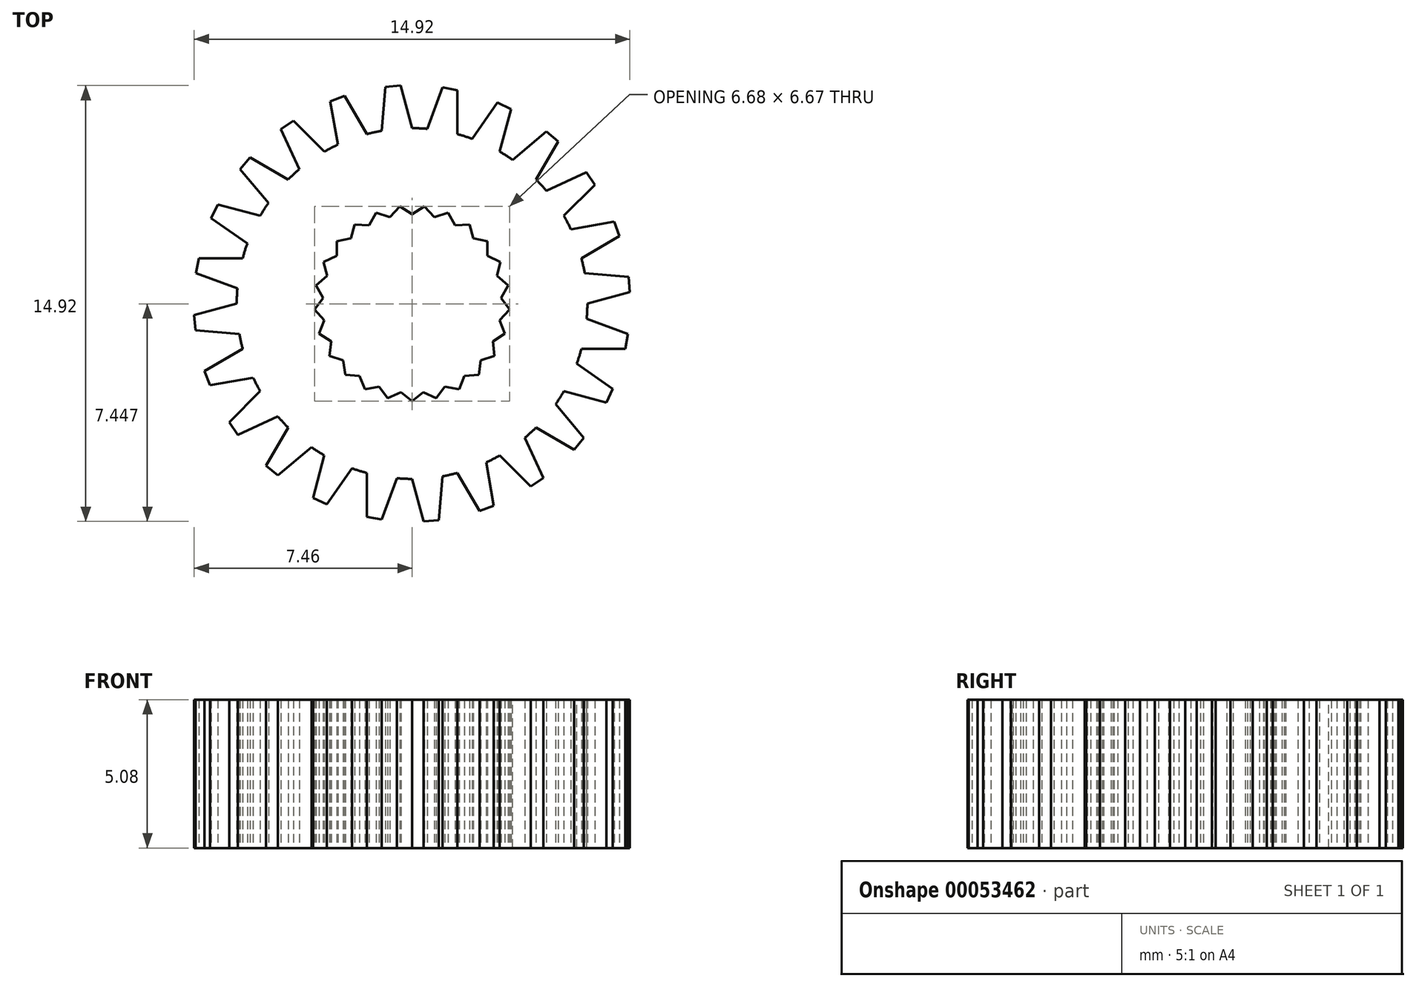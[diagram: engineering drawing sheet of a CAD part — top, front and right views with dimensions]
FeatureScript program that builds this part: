
annotation { "Feature Type Name" : "Feature", "Feature Type Description" : "" }
export const myFeature = defineFeature(function(context is Context, id is Id, definition is map)
    precondition{}
    {
        {
            var Q0;
            Q0=qCreatedBy(makeId("Top.planeOp"),FACE);
            var sketch = newSketch(context, id + "F0", { "sketchPlane" : qUnion([Q0])});
            skArc(sketch, "E0", {"start": v(0.52, 5.98) * mm, "mid": v(0.26, 6) * mm, "end": v(0, 6) * mm});
            skLineSegment(sketch, "E1", {"start": v(0, 6) * mm, "end": v(-0.39, 7.46) * mm});
            skLineSegment(sketch, "E2", {"start": v(-0.91, 7.41) * mm, "end": v(-0.39, 7.46) * mm});
            skLineSegment(sketch, "E3", {"start": v(-1.04, 5.91) * mm, "end": v(-0.91, 7.41) * mm});
            skLineSegment(sketch, "E4", {"start": v(-1.55, 5.8) * mm, "end": v(-2.3, 7.1) * mm});
            skLineSegment(sketch, "E5", {"start": v(-2.8, 6.93) * mm, "end": v(-2.3, 7.1) * mm});
            skLineSegment(sketch, "E6", {"start": v(-2.54, 5.44) * mm, "end": v(-2.8, 6.93) * mm});
            skLineSegment(sketch, "E7", {"start": v(-3, 5.2) * mm, "end": v(-4.07, 6.27) * mm});
            skLineSegment(sketch, "E8", {"start": v(-4.5, 5.97) * mm, "end": v(-4.07, 6.27) * mm});
            skLineSegment(sketch, "E9", {"start": v(-3.86, 4.6) * mm, "end": v(-4.5, 5.97) * mm});
            skLineSegment(sketch, "E10", {"start": v(-4.25, 4.25) * mm, "end": v(-5.55, 5) * mm});
            skLineSegment(sketch, "E11", {"start": v(-5.89, 4.6) * mm, "end": v(-5.55, 5) * mm});
            skLineSegment(sketch, "E12", {"start": v(-4.92, 3.44) * mm, "end": v(-5.89, 4.6) * mm});
            skLineSegment(sketch, "E13", {"start": v(-5.2, 3) * mm, "end": v(-6.66, 3.4) * mm});
            skLineSegment(sketch, "E14", {"start": v(-6.88, 2.92) * mm, "end": v(-6.66, 3.4) * mm});
            skLineSegment(sketch, "E15", {"start": v(-5.64, 2.05) * mm, "end": v(-6.88, 2.92) * mm});
            skLineSegment(sketch, "E16", {"start": v(-5.8, 1.55) * mm, "end": v(-7.3, 1.55) * mm});
            skLineSegment(sketch, "E17", {"start": v(-7.4, 1.04) * mm, "end": v(-7.3, 1.55) * mm});
            skLineSegment(sketch, "E18", {"start": v(-5.98, 0.52) * mm, "end": v(-7.4, 1.04) * mm});
            skLineSegment(sketch, "E19", {"start": v(-6, 0) * mm, "end": v(-7.46, -0.39) * mm});
            skLineSegment(sketch, "E20", {"start": v(-7.41, -0.91) * mm, "end": v(-7.46, -0.39) * mm});
            skLineSegment(sketch, "E21", {"start": v(-5.91, -1.04) * mm, "end": v(-7.41, -0.91) * mm});
            skLineSegment(sketch, "E22", {"start": v(-5.8, -1.55) * mm, "end": v(-7.1, -2.3) * mm});
            skLineSegment(sketch, "E23", {"start": v(-6.93, -2.8) * mm, "end": v(-7.1, -2.3) * mm});
            skLineSegment(sketch, "E24", {"start": v(-5.44, -2.54) * mm, "end": v(-6.93, -2.8) * mm});
            skLineSegment(sketch, "E25", {"start": v(-5.2, -3) * mm, "end": v(-6.27, -4.07) * mm});
            skLineSegment(sketch, "E26", {"start": v(-5.97, -4.5) * mm, "end": v(-6.27, -4.07) * mm});
            skLineSegment(sketch, "E27", {"start": v(-4.6, -3.86) * mm, "end": v(-5.97, -4.5) * mm});
            skLineSegment(sketch, "E28", {"start": v(-4.25, -4.25) * mm, "end": v(-5, -5.55) * mm});
            skLineSegment(sketch, "E29", {"start": v(-4.6, -5.89) * mm, "end": v(-5, -5.55) * mm});
            skLineSegment(sketch, "E30", {"start": v(-3.44, -4.92) * mm, "end": v(-4.6, -5.89) * mm});
            skLineSegment(sketch, "E31", {"start": v(-3, -5.2) * mm, "end": v(-3.4, -6.66) * mm});
            skLineSegment(sketch, "E32", {"start": v(-2.92, -6.88) * mm, "end": v(-3.4, -6.66) * mm});
            skLineSegment(sketch, "E33", {"start": v(-2.05, -5.64) * mm, "end": v(-2.92, -6.88) * mm});
            skLineSegment(sketch, "E34", {"start": v(-1.55, -5.8) * mm, "end": v(-1.55, -7.3) * mm});
            skLineSegment(sketch, "E35", {"start": v(-1.04, -7.4) * mm, "end": v(-1.55, -7.3) * mm});
            skLineSegment(sketch, "E36", {"start": v(-0.52, -5.98) * mm, "end": v(-1.04, -7.4) * mm});
            skLineSegment(sketch, "E37", {"start": v(0, -6) * mm, "end": v(0.39, -7.46) * mm});
            skLineSegment(sketch, "E38", {"start": v(0.91, -7.41) * mm, "end": v(0.39, -7.46) * mm});
            skLineSegment(sketch, "E39", {"start": v(1.04, -5.91) * mm, "end": v(0.91, -7.41) * mm});
            skLineSegment(sketch, "E40", {"start": v(1.55, -5.8) * mm, "end": v(2.3, -7.1) * mm});
            skLineSegment(sketch, "E41", {"start": v(2.8, -6.93) * mm, "end": v(2.3, -7.1) * mm});
            skLineSegment(sketch, "E42", {"start": v(2.54, -5.44) * mm, "end": v(2.8, -6.93) * mm});
            skLineSegment(sketch, "E43", {"start": v(3, -5.2) * mm, "end": v(4.07, -6.27) * mm});
            skLineSegment(sketch, "E44", {"start": v(4.5, -5.97) * mm, "end": v(4.07, -6.27) * mm});
            skLineSegment(sketch, "E45", {"start": v(3.86, -4.6) * mm, "end": v(4.5, -5.97) * mm});
            skLineSegment(sketch, "E46", {"start": v(4.25, -4.25) * mm, "end": v(5.55, -5) * mm});
            skLineSegment(sketch, "E47", {"start": v(5.89, -4.6) * mm, "end": v(5.55, -5) * mm});
            skLineSegment(sketch, "E48", {"start": v(4.92, -3.44) * mm, "end": v(5.89, -4.6) * mm});
            skLineSegment(sketch, "E49", {"start": v(5.2, -3) * mm, "end": v(6.66, -3.4) * mm});
            skLineSegment(sketch, "E50", {"start": v(6.88, -2.92) * mm, "end": v(6.66, -3.4) * mm});
            skLineSegment(sketch, "E51", {"start": v(5.64, -2.05) * mm, "end": v(6.88, -2.92) * mm});
            skLineSegment(sketch, "E52", {"start": v(5.8, -1.55) * mm, "end": v(7.3, -1.55) * mm});
            skLineSegment(sketch, "E53", {"start": v(7.4, -1.04) * mm, "end": v(7.3, -1.55) * mm});
            skLineSegment(sketch, "E54", {"start": v(5.98, -0.52) * mm, "end": v(7.4, -1.04) * mm});
            skLineSegment(sketch, "E55", {"start": v(6, 0) * mm, "end": v(7.46, 0.39) * mm});
            skLineSegment(sketch, "E56", {"start": v(7.41, 0.91) * mm, "end": v(7.46, 0.39) * mm});
            skLineSegment(sketch, "E57", {"start": v(5.91, 1.04) * mm, "end": v(7.41, 0.91) * mm});
            skLineSegment(sketch, "E58", {"start": v(5.8, 1.55) * mm, "end": v(7.1, 2.3) * mm});
            skLineSegment(sketch, "E59", {"start": v(6.93, 2.8) * mm, "end": v(7.1, 2.3) * mm});
            skLineSegment(sketch, "E60", {"start": v(5.44, 2.54) * mm, "end": v(6.93, 2.8) * mm});
            skLineSegment(sketch, "E61", {"start": v(5.2, 3) * mm, "end": v(6.27, 4.07) * mm});
            skLineSegment(sketch, "E62", {"start": v(5.97, 4.5) * mm, "end": v(6.27, 4.07) * mm});
            skLineSegment(sketch, "E63", {"start": v(4.6, 3.86) * mm, "end": v(5.97, 4.5) * mm});
            skLineSegment(sketch, "E64", {"start": v(4.25, 4.25) * mm, "end": v(5, 5.55) * mm});
            skLineSegment(sketch, "E65", {"start": v(4.6, 5.89) * mm, "end": v(5, 5.55) * mm});
            skLineSegment(sketch, "E66", {"start": v(3.44, 4.92) * mm, "end": v(4.6, 5.89) * mm});
            skLineSegment(sketch, "E67", {"start": v(3, 5.2) * mm, "end": v(3.4, 6.66) * mm});
            skLineSegment(sketch, "E68", {"start": v(2.92, 6.88) * mm, "end": v(3.4, 6.66) * mm});
            skLineSegment(sketch, "E69", {"start": v(2.05, 5.64) * mm, "end": v(2.92, 6.88) * mm});
            skLineSegment(sketch, "E70", {"start": v(1.55, 5.8) * mm, "end": v(1.55, 7.3) * mm});
            skLineSegment(sketch, "E71", {"start": v(1.04, 7.4) * mm, "end": v(1.55, 7.3) * mm});
            skLineSegment(sketch, "E72", {"start": v(0.52, 5.98) * mm, "end": v(1.04, 7.4) * mm});
            skArc(sketch, "E73", {"start": v(2.05, 5.64) * mm, "mid": v(1.8, 5.73) * mm, "end": v(1.55, 5.8) * mm});
            skArc(sketch, "E74", {"start": v(3.44, 4.92) * mm, "mid": v(3.23, 5.06) * mm, "end": v(3, 5.2) * mm});
            skArc(sketch, "E75", {"start": v(4.6, 3.86) * mm, "mid": v(4.43, 4.06) * mm, "end": v(4.25, 4.25) * mm});
            skArc(sketch, "E76", {"start": v(5.44, 2.54) * mm, "mid": v(5.33, 2.77) * mm, "end": v(5.2, 3) * mm});
            skArc(sketch, "E77", {"start": v(5.91, 1.04) * mm, "mid": v(5.86, 1.3) * mm, "end": v(5.8, 1.55) * mm});
            skArc(sketch, "E78", {"start": v(5.98, -0.52) * mm, "mid": v(6, -0.26) * mm, "end": v(6, 0) * mm});
            skArc(sketch, "E79", {"start": v(5.64, -2.05) * mm, "mid": v(5.73, -1.8) * mm, "end": v(5.8, -1.55) * mm});
            skArc(sketch, "E80", {"start": v(4.92, -3.44) * mm, "mid": v(5.06, -3.23) * mm, "end": v(5.2, -3) * mm});
            skArc(sketch, "E81", {"start": v(3.86, -4.6) * mm, "mid": v(4.06, -4.43) * mm, "end": v(4.25, -4.25) * mm});
            skArc(sketch, "E82", {"start": v(2.54, -5.44) * mm, "mid": v(2.77, -5.33) * mm, "end": v(3, -5.2) * mm});
            skArc(sketch, "E83", {"start": v(1.04, -5.91) * mm, "mid": v(1.3, -5.86) * mm, "end": v(1.55, -5.8) * mm});
            skArc(sketch, "E84", {"start": v(-0.52, -5.98) * mm, "mid": v(-0.26, -6) * mm, "end": v(0, -6) * mm});
            skArc(sketch, "E85", {"start": v(-2.05, -5.64) * mm, "mid": v(-1.8, -5.73) * mm, "end": v(-1.55, -5.8) * mm});
            skArc(sketch, "E86", {"start": v(-3.44, -4.92) * mm, "mid": v(-3.23, -5.06) * mm, "end": v(-3, -5.2) * mm});
            skArc(sketch, "E87", {"start": v(-4.6, -3.86) * mm, "mid": v(-4.43, -4.06) * mm, "end": v(-4.25, -4.25) * mm});
            skArc(sketch, "E88", {"start": v(-5.44, -2.54) * mm, "mid": v(-5.33, -2.77) * mm, "end": v(-5.2, -3) * mm});
            skArc(sketch, "E89", {"start": v(-5.91, -1.04) * mm, "mid": v(-5.86, -1.3) * mm, "end": v(-5.8, -1.55) * mm});
            skArc(sketch, "E90", {"start": v(-5.98, 0.52) * mm, "mid": v(-6, 0.26) * mm, "end": v(-6, 0) * mm});
            skArc(sketch, "E91", {"start": v(-5.64, 2.05) * mm, "mid": v(-5.73, 1.8) * mm, "end": v(-5.8, 1.55) * mm});
            skArc(sketch, "E92", {"start": v(-1.04, 5.91) * mm, "mid": v(-1.3, 5.86) * mm, "end": v(-1.55, 5.8) * mm});
            skArc(sketch, "E93", {"start": v(-2.54, 5.44) * mm, "mid": v(-2.77, 5.33) * mm, "end": v(-3, 5.2) * mm});
            skArc(sketch, "E94", {"start": v(-3.86, 4.6) * mm, "mid": v(-4.06, 4.43) * mm, "end": v(-4.25, 4.25) * mm});
            skArc(sketch, "E95", {"start": v(-4.92, 3.44) * mm, "mid": v(-5.06, 3.23) * mm, "end": v(-5.2, 3) * mm});
            skLineSegment(sketch, "E96", {"start": v(-0.76, 2.96) * mm, "end": v(-0.42, 3.32) * mm});
            skLineSegment(sketch, "E97", {"start": v(-0.42, 3.32) * mm, "end": v(0, 3.06) * mm});
            skLineSegment(sketch, "E98", {"start": v(-1.47, 2.68) * mm, "end": v(-1.23, 3.11) * mm});
            skLineSegment(sketch, "E99", {"start": v(-1.23, 3.11) * mm, "end": v(-0.76, 2.96) * mm});
            skLineSegment(sketch, "E100", {"start": v(-2.1, 2.23) * mm, "end": v(-1.97, 2.7) * mm});
            skLineSegment(sketch, "E101", {"start": v(-1.97, 2.7) * mm, "end": v(-1.47, 2.68) * mm});
            skLineSegment(sketch, "E102", {"start": v(-2.58, 1.64) * mm, "end": v(-2.58, 2.13) * mm});
            skLineSegment(sketch, "E103", {"start": v(-2.58, 2.13) * mm, "end": v(-2.1, 2.23) * mm});
            skLineSegment(sketch, "E104", {"start": v(-2.9, 0.95) * mm, "end": v(-3.03, 1.42) * mm});
            skLineSegment(sketch, "E105", {"start": v(-3.03, 1.42) * mm, "end": v(-2.58, 1.64) * mm});
            skLineSegment(sketch, "E106", {"start": v(-3.05, 0.2) * mm, "end": v(-3.29, 0.63) * mm});
            skLineSegment(sketch, "E107", {"start": v(-3.29, 0.63) * mm, "end": v(-2.9, 0.95) * mm});
            skLineSegment(sketch, "E108", {"start": v(-3, -0.57) * mm, "end": v(-3.34, -0.21) * mm});
            skLineSegment(sketch, "E109", {"start": v(-3.34, -0.21) * mm, "end": v(-3.05, 0.2) * mm});
            skLineSegment(sketch, "E110", {"start": v(-2.77, -1.3) * mm, "end": v(-3.18, -1.03) * mm});
            skLineSegment(sketch, "E111", {"start": v(-3.18, -1.03) * mm, "end": v(-3, -0.57) * mm});
            skLineSegment(sketch, "E112", {"start": v(-2.36, -1.95) * mm, "end": v(-2.83, -1.8) * mm});
            skLineSegment(sketch, "E113", {"start": v(-2.83, -1.8) * mm, "end": v(-2.77, -1.3) * mm});
            skLineSegment(sketch, "E114", {"start": v(-1.8, -2.47) * mm, "end": v(-2.3, -2.44) * mm});
            skLineSegment(sketch, "E115", {"start": v(-2.3, -2.44) * mm, "end": v(-2.36, -1.95) * mm});
            skLineSegment(sketch, "E116", {"start": v(-1.13, -2.84) * mm, "end": v(-1.61, -2.93) * mm});
            skLineSegment(sketch, "E117", {"start": v(-1.61, -2.93) * mm, "end": v(-1.8, -2.47) * mm});
            skLineSegment(sketch, "E118", {"start": v(-0.38, -3.03) * mm, "end": v(-0.83, -3.24) * mm});
            skLineSegment(sketch, "E119", {"start": v(-0.83, -3.24) * mm, "end": v(-1.13, -2.84) * mm});
            skLineSegment(sketch, "E120", {"start": v(0.38, -3.03) * mm, "end": v(0, -3.35) * mm});
            skLineSegment(sketch, "E121", {"start": v(0, -3.35) * mm, "end": v(-0.38, -3.03) * mm});
            skLineSegment(sketch, "E122", {"start": v(1.13, -2.84) * mm, "end": v(0.83, -3.24) * mm});
            skLineSegment(sketch, "E123", {"start": v(0.83, -3.24) * mm, "end": v(0.38, -3.03) * mm});
            skLineSegment(sketch, "E124", {"start": v(1.8, -2.47) * mm, "end": v(1.61, -2.93) * mm});
            skLineSegment(sketch, "E125", {"start": v(1.61, -2.93) * mm, "end": v(1.13, -2.84) * mm});
            skLineSegment(sketch, "E126", {"start": v(2.36, -1.95) * mm, "end": v(2.3, -2.44) * mm});
            skLineSegment(sketch, "E127", {"start": v(2.3, -2.44) * mm, "end": v(1.8, -2.47) * mm});
            skLineSegment(sketch, "E128", {"start": v(2.77, -1.3) * mm, "end": v(2.83, -1.8) * mm});
            skLineSegment(sketch, "E129", {"start": v(2.83, -1.8) * mm, "end": v(2.36, -1.95) * mm});
            skLineSegment(sketch, "E130", {"start": v(3, -0.57) * mm, "end": v(3.18, -1.03) * mm});
            skLineSegment(sketch, "E131", {"start": v(3.18, -1.03) * mm, "end": v(2.77, -1.3) * mm});
            skLineSegment(sketch, "E132", {"start": v(3.05, 0.2) * mm, "end": v(3.34, -0.21) * mm});
            skLineSegment(sketch, "E133", {"start": v(3.34, -0.21) * mm, "end": v(3, -0.57) * mm});
            skLineSegment(sketch, "E134", {"start": v(2.9, 0.95) * mm, "end": v(3.29, 0.63) * mm});
            skLineSegment(sketch, "E135", {"start": v(3.29, 0.63) * mm, "end": v(3.05, 0.2) * mm});
            skLineSegment(sketch, "E136", {"start": v(2.58, 1.64) * mm, "end": v(3.03, 1.42) * mm});
            skLineSegment(sketch, "E137", {"start": v(3.03, 1.42) * mm, "end": v(2.9, 0.95) * mm});
            skLineSegment(sketch, "E138", {"start": v(2.1, 2.23) * mm, "end": v(2.58, 2.13) * mm});
            skLineSegment(sketch, "E139", {"start": v(2.58, 2.13) * mm, "end": v(2.58, 1.64) * mm});
            skLineSegment(sketch, "E140", {"start": v(1.47, 2.68) * mm, "end": v(1.97, 2.7) * mm});
            skLineSegment(sketch, "E141", {"start": v(1.97, 2.7) * mm, "end": v(2.1, 2.23) * mm});
            skLineSegment(sketch, "E142", {"start": v(0.76, 2.96) * mm, "end": v(1.23, 3.11) * mm});
            skLineSegment(sketch, "E143", {"start": v(1.23, 3.11) * mm, "end": v(1.47, 2.68) * mm});
            skLineSegment(sketch, "E144", {"start": v(0, 3.06) * mm, "end": v(0.42, 3.32) * mm});
            skLineSegment(sketch, "E145", {"start": v(0.42, 3.32) * mm, "end": v(0.76, 2.96) * mm});
            skSolve(sketch);
        }
        {
            var Q0;
            Q0=makeQuery(id+"F0.imprint","IMPRINT",FACE,{"disambiguationData":[TD([[makeQuery(id+"F0.imprint","IMPRINT",EDGE,{"derivedFrom":sQuery(id+"F0.wireOp",EDGE,"E0")}),1.0]])]});
            extrude(context, id + "F1", {"entities" : qUnion([Q0]), "depth" : 5.08 * mm});
        }
    });
